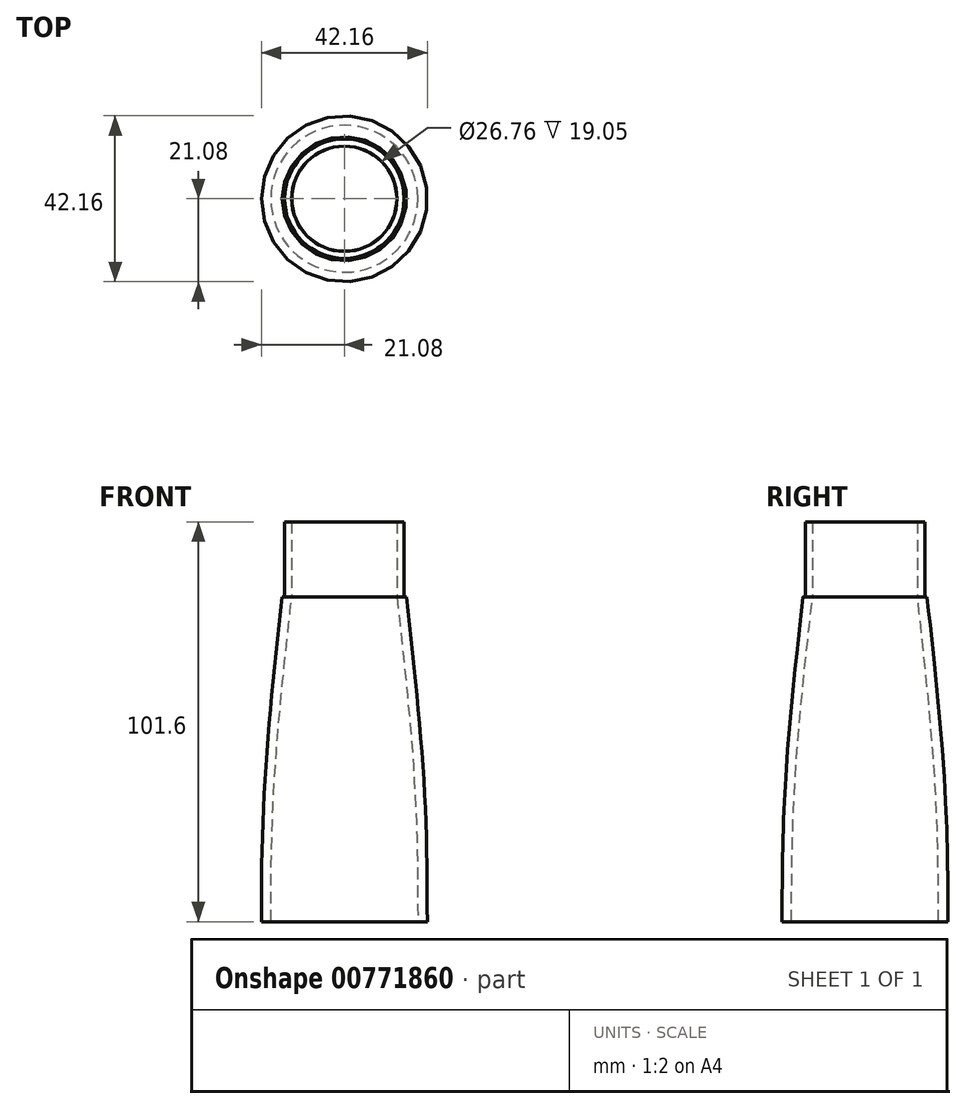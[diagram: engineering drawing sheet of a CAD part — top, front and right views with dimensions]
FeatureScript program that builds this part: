
annotation { "Feature Type Name" : "Feature", "Feature Type Description" : "" }
export const myFeature = defineFeature(function(context is Context, id is Id, definition is map)
    precondition{}
    {
        {
            var Q0;
            Q0=qCreatedBy(makeId("Top.planeOp"),FACE);
            var sketch = newSketch(context, id + "F0", { "sketchPlane" : qUnion([Q0])});
            skCircle(sketch, "E0", {"center": v(0, 0) * mm, "radius": 18.29 * mm});
            skSolve(sketch);
        }
        {
            var Q0;
            Q0=qCreatedBy(makeId("Top.planeOp"),FACE);
            cPlane(context, id + "F1", {"entities" : qUnion([Q0]), "cplaneType" : CPlaneType.OFFSET, "offset" : 57.15 * mm, "width" : 152.4 * mm, "height" : 152.4 * mm});
        }
        {
            var Q0;
            Q0=qCreatedBy(id+"F1.planeOp",FACE);
            var sketch = newSketch(context, id + "F2", { "sketchPlane" : qUnion([Q0])});
            skCircle(sketch, "E1", {"center": v(0, 0) * mm, "radius": 13.33 * mm});
            skSolve(sketch);
        }
        {
            var Q0;
            Q0=qCreatedBy(makeId("Top.planeOp"),FACE);
            cPlane(context, id + "F3", {"entities" : qUnion([Q0]), "cplaneType" : CPlaneType.OFFSET, "offset" : 25.4 * mm, "oppositeDirection" : true, "width" : 152.4 * mm, "height" : 152.4 * mm});
        }
        {
            var Q0;
            Q0=qCreatedBy(id+"F3.planeOp",FACE);
            var sketch = newSketch(context, id + "F4", { "sketchPlane" : qUnion([Q0])});
            skCircle(sketch, "E2", {"center": v(0, 0) * mm, "radius": 18.67 * mm});
            skSolve(sketch);
        }
        {
            var Q0;
            Q0=makeQuery(id+"F2.imprint","IMPRINT",FACE,{"disambiguationData":[TD([[makeQuery(id+"F2.imprint","IMPRINT",EDGE,{"derivedFrom":sQuery(id+"F2.wireOp",EDGE,"E1")}),1.0]])]});
            var Q1;
            Q1=makeQuery(id+"F0.imprint","IMPRINT",FACE,{"disambiguationData":[TD([[makeQuery(id+"F0.imprint","IMPRINT",EDGE,{"derivedFrom":sQuery(id+"F0.wireOp",EDGE,"E0")}),1.0]])]});
            var Q2;
            Q2=makeQuery(id+"F4.imprint","IMPRINT",FACE,{"disambiguationData":[TD([[makeQuery(id+"F4.imprint","IMPRINT",EDGE,{"derivedFrom":sQuery(id+"F4.wireOp",EDGE,"E2")}),1.0]])]});
            loft(context, id + "F5", {"sheetProfilesArray" : [{ "sheetProfileEntities" : qUnion([Q0]) }, { "sheetProfileEntities" : qUnion([Q1]) }, { "sheetProfileEntities" : qUnion([Q2]) }]});
        }
        {
            var Q0;
            Q0=makeQuery(id+"F5.opLoft","CAP_FACE",FACE,{"disambiguationData":[OSD([makeQuery(id+"F4.imprint","IMPRINT",FACE,{"disambiguationData":[TD([[makeQuery(id+"F4.imprint","IMPRINT",EDGE,{"derivedFrom":sQuery(id+"F4.wireOp",EDGE,"E2")}),1.0]])]})])],"isStart":true});
            var Q1;
            Q1=makeQuery(id+"F5.opLoft","CAP_FACE",FACE,{"disambiguationData":[OSD([makeQuery(id+"F2.imprint","IMPRINT",FACE,{"disambiguationData":[TD([[makeQuery(id+"F2.imprint","IMPRINT",EDGE,{"derivedFrom":sQuery(id+"F2.wireOp",EDGE,"E1")}),1.0]])]})])],"isStart":true});
            shell(context, id + "F6", {"entities" : qUnion([Q0, Q1]), "thickness" : 2.41 * mm, "oppositeDirection" : true});
        }
        {
            var Q0;
            Q0=qCreatedBy(id+"F1.planeOp",FACE);
            var sketch = newSketch(context, id + "F7", { "sketchPlane" : qUnion([Q0])});
            skCircle(sketch, "E3", {"center": v(0, 0) * mm, "radius": 15.18 * mm});
            skCircle(sketch, "E4", {"center": v(0, 0) * mm, "radius": 13.38 * mm});
            skSolve(sketch);
        }
        {
            var Q0;
            Q0=makeQuery(id+"F7.imprint","IMPRINT",FACE,{"disambiguationData":[TD([[makeQuery(id+"F7.imprint","IMPRINT",EDGE,{"derivedFrom":sQuery(id+"F7.wireOp",EDGE,"E3")}),1.0]])]});
            extrude(context, id + "F8", {"entities" : qUnion([Q0]), "operationType" : NewBodyOperationType.ADD, "depth" : 19.05 * mm, "offsetDistance" : 25.4 * mm});
        }
    });
